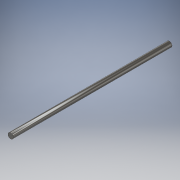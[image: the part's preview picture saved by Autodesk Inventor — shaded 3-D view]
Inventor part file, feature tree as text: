
AUTODESK INVENTOR PART (.ipt)
format: ipt  version: 2017 (Build 210142000, 142)  size: 92,672 bytes
history: native  units: in
note: dims shown in document units (in); Inventor stores cm internally (conversion verified against a paired STEP export)
features: extrude x1, sketch x1
ambient origin geometry x8: Origin, YZ Plane, XZ Plane, XY Plane, X Axis, Y Axis, Z Axis, Center Point
bodies: Solid1 (feature_tree)
feature tree (2):
  extrude  "Extrusion1"  Depth=3.45in TaperAngle=0.0deg
  sketch  "Sketch1"  dims[d0=0.1181in d1=3.45in d2=0.0in]
